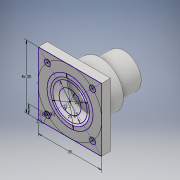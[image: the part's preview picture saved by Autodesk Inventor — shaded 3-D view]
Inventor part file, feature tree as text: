
AUTODESK INVENTOR PART (.ipt)
format: ipt  version: 2018 (Build 220112000, 112)  size: 145,920 bytes
history: native  units: mm
features: extrude x4, sketch x1
ambient origin geometry x8: Origin, YZ Plane, XZ Plane, XY Plane, X Axis, Y Axis, Z Axis, Center Point
bodies: Solid1 (feature_tree)
feature tree (5):
  sketch  "Sketch1"  dims[d0=35.0mm d1=35.0mm d2=3.3mm d3=5.0mm d4=40.0mm d6=360.0deg d8=12.1mm d9=19.0mm d10=5.0mm d11=0.0mm d12=30.0mm d13=0.0mm d14=25.4mm d15=17.0mm d16=0.0mm d17=21.4mm d18=10.0mm d19=0.0mm]
  extrude  "Extrusion1"  Depth=35.0mm
  extrude  "Extrusion2"  Depth=10.0mm
  extrude  "Extrusion3"  Depth=5.0mm
  extrude  "Extrusion4"  Depth=10.0mm TaperAngle=360.0deg
